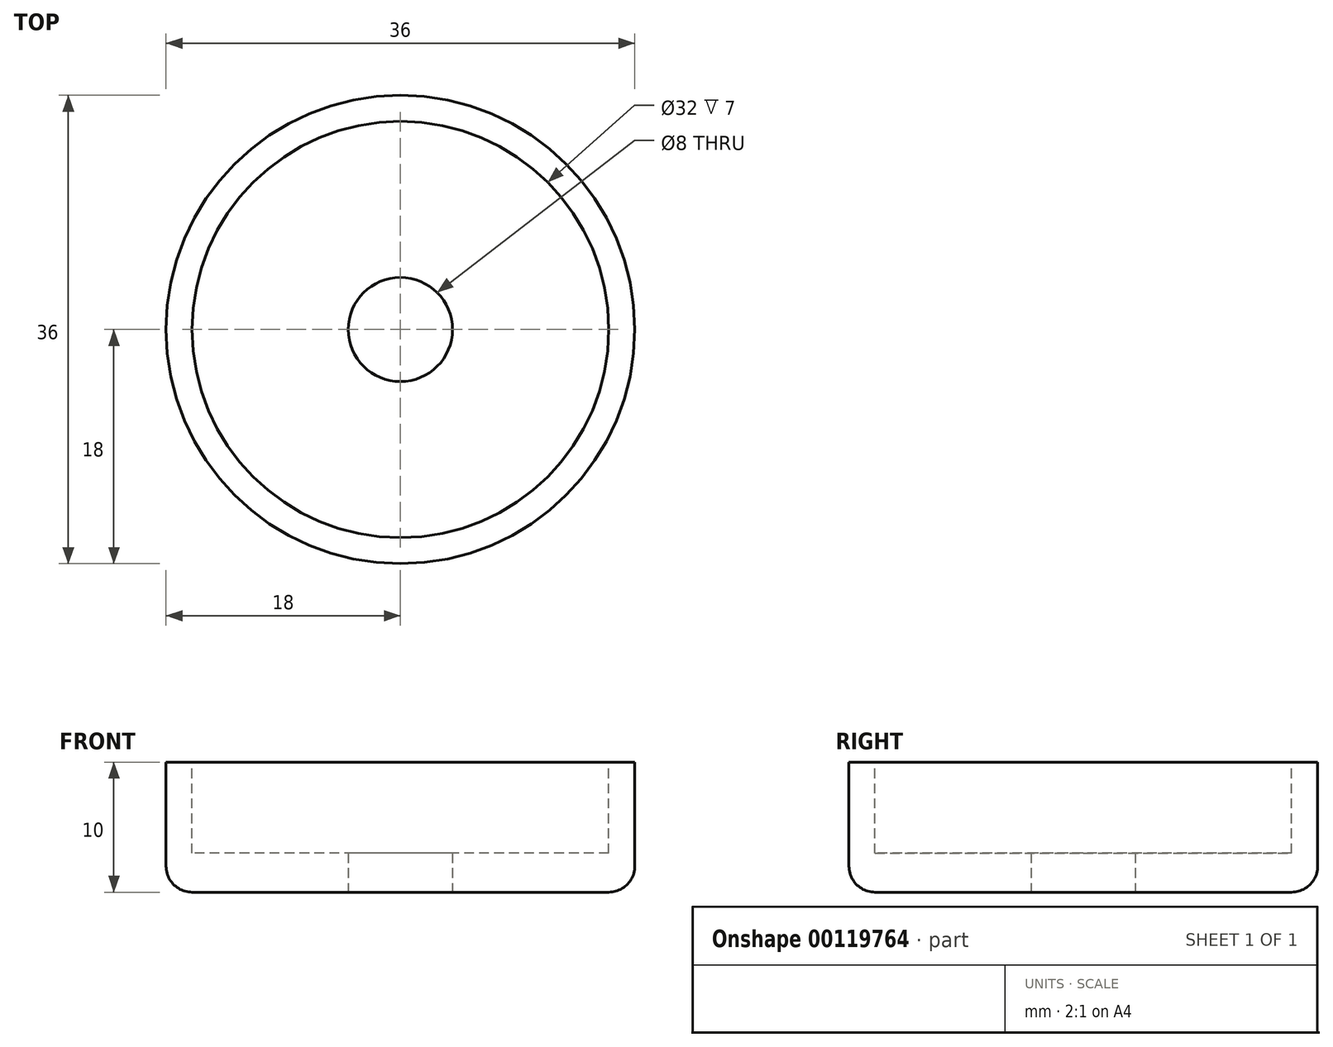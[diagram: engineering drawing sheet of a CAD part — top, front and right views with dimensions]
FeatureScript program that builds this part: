
annotation { "Feature Type Name" : "Feature", "Feature Type Description" : "" }
export const myFeature = defineFeature(function(context is Context, id is Id, definition is map)
    precondition{}
    {
        {
            var Q0;
            Q0=qCreatedBy(makeId("Top.planeOp"),FACE);
            var sketch = newSketch(context, id + "F0", { "sketchPlane" : qUnion([Q0])});
            skCircle(sketch, "E0", {"center": v(0, 0) * mm, "radius": 18 * mm});
            skSolve(sketch);
        }
        {
            var Q0;
            Q0 = qSketchRegion(id + "F0", true);
            extrude(context, id + "F1", {"entities" : qUnion([Q0]), "depth" : 10 * mm});
        }
        {
            var Q0;
            Q0=makeQuery(id+"F1.opExtrude","CAP_FACE",FACE,{"disambiguationData":[OSD([sQuery(id+"F0.wireOp",EDGE,"E0")])],"isStart":false});
            var sketch = newSketch(context, id + "F2", { "sketchPlane" : qUnion([Q0])});
            skCircle(sketch, "E1", {"center": v(0, 0) * mm, "radius": 16 * mm});
            skSolve(sketch);
        }
        {
            var Q0;
            Q0 = qSketchRegion(id + "F2", true);
            extrude(context, id + "F3", {"entities" : qUnion([Q0]), "operationType" : NewBodyOperationType.REMOVE, "oppositeDirection" : true, "depth" : 7 * mm});
        }
        {
            var Q0;
            Q0=makeQuery(id+"F1.opExtrude","CAP_FACE",FACE,{"disambiguationData":[OSD([sQuery(id+"F0.wireOp",EDGE,"E0")])],"isStart":true});
            var sketch = newSketch(context, id + "F4", { "sketchPlane" : qUnion([Q0])});
            skCircle(sketch, "E2", {"center": v(0, 0) * mm, "radius": 4 * mm});
            skSolve(sketch);
        }
        {
            var Q0;
            Q0 = qSketchRegion(id + "F4", true);
            extrude(context, id + "F5", {"entities" : qUnion([Q0]), "operationType" : NewBodyOperationType.REMOVE, "oppositeDirection" : true, "depth" : 25 * mm});
        }
        {
            var Q0;
            Q0=makeQuery(id+"F1.opExtrude","CAP_EDGE",EDGE,{"disambiguationData":[OSD([sQuery(id+"F0.wireOp",EDGE,"E0")])],"isStart":true});
            fillet(context, id + "F6", {"entities" : qUnion([Q0]), "radius" : 2 * mm, "tangentPropagation" : true, "allowEdgeOverflow" : false});
        }
    });
